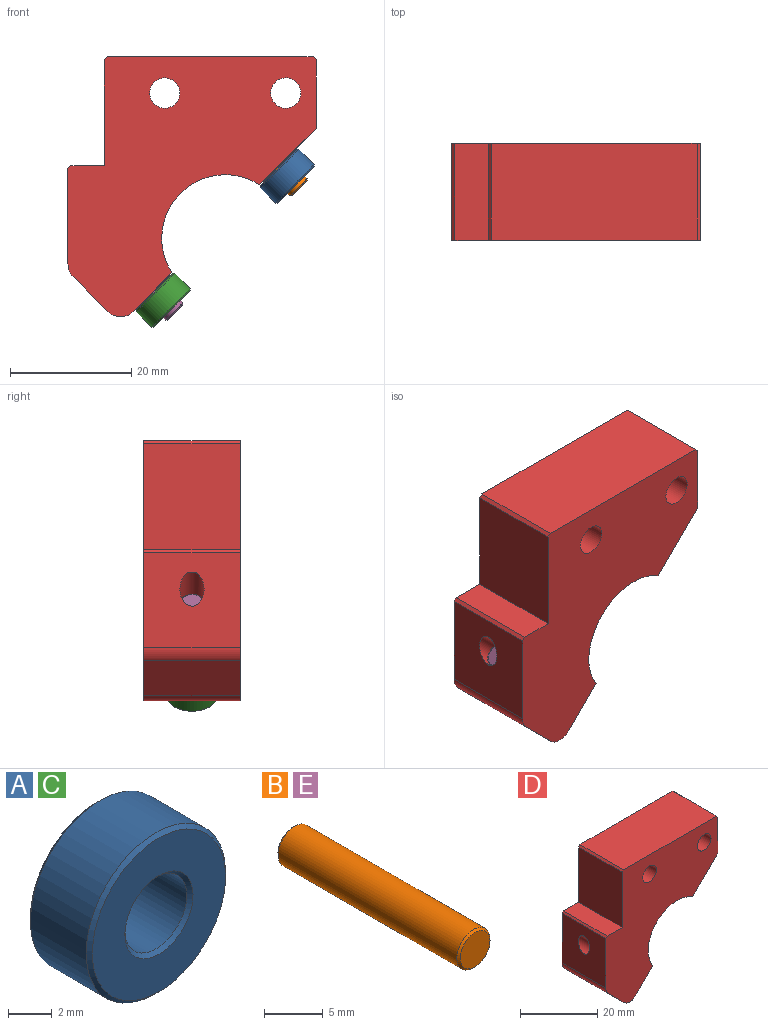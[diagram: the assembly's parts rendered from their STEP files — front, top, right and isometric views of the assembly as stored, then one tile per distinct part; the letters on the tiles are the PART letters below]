
ASSEMBLY  parts=5 mates=4
PART A: 8 faces, bbox 9x4x9 mm
  f0: cylinder r=2mm len=4mm, axis (0,1,0), area 45.2mm2, adj f4,f5
  f1: cylinder r=4.5mm len=9mm, axis (0,1,0), area 101.8mm2, adj f6,f7
  f2: plane 8.6x8.6mm, normal (0,-1,0), area 42.9mm2, adj f5,f7
  f3: plane 8.6x8.6mm, normal (0,1,0), area 42.9mm2, adj f4,f6
  f4: cone r=2.2mm half-angle=45deg, axis (0,1,0), area 3.7mm2, adj f0,f3
  f5: cone r=2mm half-angle=45deg, axis (0,-1,0), area 3.7mm2, adj f0,f2
  f6: cone r=4.5mm half-angle=45deg, axis (0,-1,0), area 7.8mm2, adj f1,f3
  f7: cone r=4.3mm half-angle=45deg, axis (0,1,0), area 7.8mm2, adj f1,f2
PART B: 5 faces, bbox 4x22x4 mm
  f0: cylinder r=2mm len=21.6mm, axis (0,1,0), area 271.4mm2, adj f3,f4
  f1: plane 3.6x3.6mm, normal (0,-1,0), area 10.2mm2, adj f4
  f2: plane 3.6x3.6mm, normal (0,1,0), area 10.2mm2, adj f3
  f3: cone r=2mm half-angle=45deg, axis (0,-1,0), area 3.4mm2, adj f0,f2
  f4: cone r=1.8mm half-angle=45deg, axis (0,1,0), area 3.4mm2, adj f0,f1
PART C: same geometry as A
PART D: 22 faces, bbox 43.8x16x42.9 mm
  f0: plane 16x15.75mm, normal (-1,0,0), area 234.3mm2, adj f11,f12,f14,f15,f18,f19
  f1: plane 16x5.7mm, normal (-0.71,0,-0.71), area 129mm2, adj f11,f12,f13,f14
  f2: plane 16x6.36mm, normal (0.71,0,-0.71), area 131.4mm2, adj f3,f11,f12,f13,f18
  f3: cylinder r=10.5mm len=16.2mm, axis (0,-1,0), area 456.9mm2, adj f2,f4,f11,f12
  f4: plane 16x9.3mm, normal (0.71,0,-0.71), area 197.8mm2, adj f3,f5,f11,f12,f20
  f5: plane 16x11.39mm, normal (1,0,0), area 182.2mm2, adj f4,f11,f12,f17
  f6: plane 34x16mm, normal (0,0,1), area 544mm2, adj f11,f12,f16,f17
  f7: plane 17.5x16mm, normal (-1,0,0), area 280mm2, adj f8,f11,f12,f16
  f8: plane 16x5.5mm, normal (0,0,1), area 88mm2, adj f7,f11,f12,f15
  f9: cylinder r=2.5mm len=16mm, axis (0,-1,0), area 251.3mm2, adj f11,f12
  f10: cylinder r=2.5mm len=16mm, axis (0,-1,0), area 251.3mm2, adj f11,f12
  f11: plane 42.95x41mm, normal (0,1,0), area 975.2mm2, adj f0,f1,f2,f3,f4,f5,f6,f7
  f12: plane 42.95x41mm, normal (0,-1,0), area 975.2mm2, adj f0,f1,f2,f3,f4,f5,f6,f7
  f13: cylinder r=3mm len=16mm, axis (0,-1,0), area 75.4mm2, adj f1,f2,f11,f12
  f14: cylinder r=3mm len=16mm, axis (0,1,0), area 37.7mm2, adj f0,f1,f11,f12
  f15: plane 16x0.5mm, normal (-0.71,0,0.71), area 11.3mm2, adj f0,f8,f11,f12
  f16: plane 16x0.5mm, normal (-0.71,0,0.71), area 11.3mm2, adj f6,f7,f11,f12
  f17: plane 16x0.5mm, normal (0.71,0,0.71), area 11.3mm2, adj f5,f6,f11,f12
  f18: cylinder r=2mm len=18.38mm, axis (0.71,0,-0.71), area 252.2mm2, adj f0,f2,f19
  f19: plane 1.05x0.05mm, normal (0.71,0,-0.71), area 0mm2, adj f0,f18
  f20: cylinder r=2mm len=18.38mm, axis (0.71,0,-0.71), area 276.5mm2, adj f4,f21
  f21: plane 4x2.83mm, normal (0.71,0,-0.71), area 12.6mm2, adj f20
PART E: same geometry as B
PLACE A rot(axis=(-0.68,-0.68,0.28),148.6deg) t=(11.67,8,8.84)mm
PLACE B rot(axis=(-0.68,-0.68,0.28),148.6deg) t=(12.23,8,8.27)mm
PLACE C rot(axis=(-0.68,-0.68,0.28),148.6deg) t=(-8.84,8,-11.67)mm
PLACE D at identity
PLACE E rot(axis=(-0.86,-0.36,-0.36),98.4deg) t=(-8.27,8,-12.23)mm
MATE fastened C.f0 <-> D.f18  axis (-0.71,0,0.71) through (-11.67,8,-8.84)mm
MATE fastened A.f0 <-> D.f20  axis (-0.71,0,0.71) through (8.84,8,11.67)mm
MATE fastened E.f0 <-> D.f18  axis (-0.71,0,0.71) through (-23.83,8,3.32)mm
MATE fastened B.f0 <-> D.f20  axis (-0.71,0,0.71) through (-3.32,8,23.83)mm
